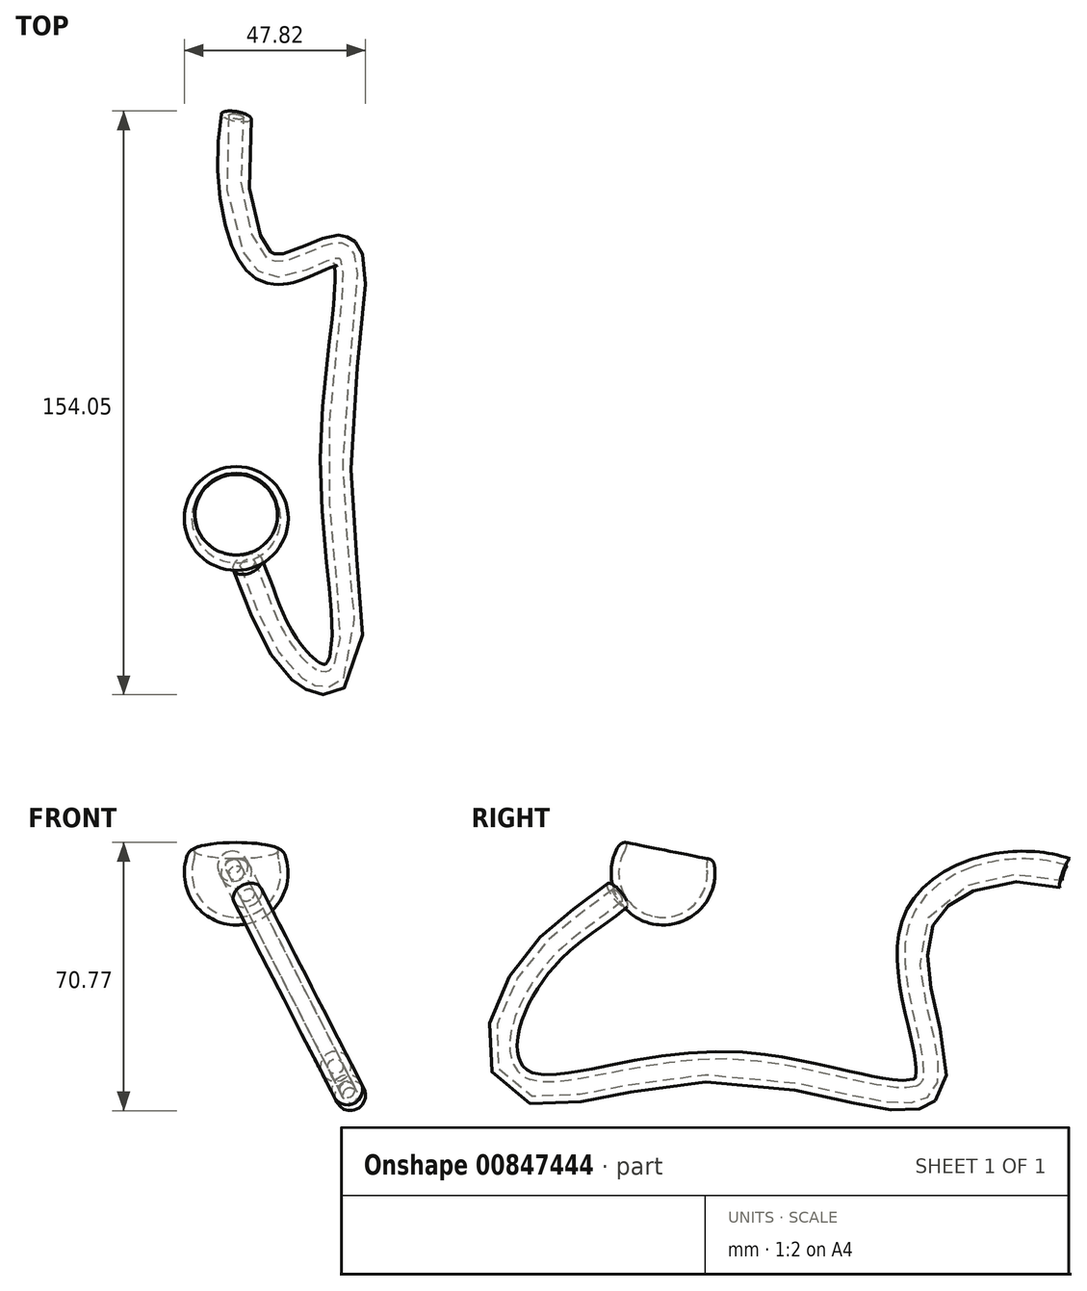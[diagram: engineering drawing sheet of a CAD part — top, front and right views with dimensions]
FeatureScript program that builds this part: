
annotation { "Feature Type Name" : "Feature", "Feature Type Description" : "" }
export const myFeature = defineFeature(function(context is Context, id is Id, definition is map)
    precondition{}
    {
        {
            var Q0;
            Q0=qCreatedBy(makeId("Right.planeOp"),FACE);
            var sketch = newSketch(context, id + "F0", { "sketchPlane" : qUnion([Q0])});
            skArc(sketch, "E0", {"start": v(-39.77, 2.1) * mm, "mid": v(-55.97, -13.44) * mm, "end": v(-65.04, 7.1) * mm});
            skLineSegment(sketch, "E1", {"start": v(-62.94, 8.02) * mm, "end": v(-41.36, 3.75) * mm});
            skPoint(sketch, "E2.visualSharp", {"position": v(-64.23, 8.28) * mm});
            skArc(sketch, "E2.filletArc", {"start": v(-62.94, 8.02) * mm, "mid": v(-64.13, 7.89) * mm, "end": v(-65.04, 7.1) * mm});
            skPoint(sketch, "E3.visualSharp", {"position": v(-40.06, 3.5) * mm});
            skArc(sketch, "E3.filletArc", {"start": v(-39.77, 2.1) * mm, "mid": v(-40.3, 3.17) * mm, "end": v(-41.36, 3.75) * mm});
            skLineSegment(sketch, "E4", {"start": v(-53.31, 0) * mm, "end": v(-55.97, -13.44) * mm, "construction": true});
            skLineSegment(sketch, "E5", {"start": v(-52.15, 5.89) * mm, "end": v(-55.97, -13.44) * mm});
            skSolve(sketch);
        }
        {
            var Q0;
            {var subQ0=sQuery(id+"F0.wireOp",EDGE,"E3.filletArc");Q0=makeQuery(id+"F0.imprint","IMPRINT",FACE,{"disambiguationData":[TD([[makeQuery(id+"F0.imprint","IMPRINT",EDGE,{"derivedFrom":subQ0}),1.0]])]});}
            var Q1;
            Q1=sQuery(id+"F0.wireOp",EDGE,"E5");
            revolve(context, id + "F1", {"surfaceOperationType" : NewSurfaceOperationType.NEW, "entities" : qUnion([Q0]), "axis" : qUnion([Q1]), "revolveType" : RevolveType.FULL});
        }
        {
            var Q0;
            Q0=makeQuery(id+"F1.opRevolve","SWEPT_FACE",FACE,{"disambiguationData":[OSD([sQuery(id+"F0.wireOp",EDGE,"E1")])]});
            shell(context, id + "F2", {"entities" : qUnion([Q0]), "thickness" : 2 * mm});
        }
        {
            var Q0;
            Q0=makeQuery(id+"F2.opShell","OFFSET_EDGE",EDGE,{"disambiguationData":[OSD([sQuery(id+"F0.wireOp",EDGE,"E0"),sQuery(id+"F0.wireOp",EDGE,"E1"),sQuery(id+"F0.wireOp",EDGE,"E3.filletArc")])]});
            fillet(context, id + "F3", {"entities" : qUnion([Q0]), "radius" : 5 * mm, "tangentPropagation" : true, "allowEdgeOverflow" : false});
        }
        {
            var Q0;
            Q0=qCreatedBy(makeId("Front.planeOp"),FACE);
            var sketch = newSketch(context, id + "F4", { "sketchPlane" : qUnion([Q0])});
            skLineSegment(sketch, "E6", {"start": v(19.4, 37.82) * mm, "end": v(-19.4, -37.82) * mm});
            skLineSegment(sketch, "E7", {"start": v(-19.4, 37.82) * mm, "end": v(19.4, -37.82) * mm});
            skPoint(sketch, "E8", {"position": v(0, 0) * mm});
            skSolve(sketch);
        }
        {
            var Q0;
            Q0=sQuery(id+"F4.wireOp",EDGE,"E7");
            cPlane(context, id + "F5", {"entities" : qUnion([Q0]), "cplaneType" : CPlaneType.LINE_ANGLE, "offset" : 25 * mm, "angle" : 0 * degree, "width" : 150 * mm, "height" : 150 * mm});
        }
        {
            var Q0;
            Q0=qCreatedBy(makeId("Right.planeOp"),FACE);
            var sketch = newSketch(context, id + "F6", { "sketchPlane" : qUnion([Q0])});
            skLineSegment(sketch, "E9", {"start": v(-100.5, -56.65) * mm, "end": v(83.38, -56.65) * mm});
            skSolve(sketch);
        }
        {
            var Q0;
            Q0=sQuery(id+"F6.wireOp",EDGE,"E9");
            cPlane(context, id + "F7", {"entities" : qUnion([Q0]), "cplaneType" : CPlaneType.LINE_ANGLE, "offset" : 25 * mm, "angle" : 0 * degree, "width" : 150 * mm, "height" : 150 * mm});
        }
        {
            var Q0;
            Q0=qCreatedBy(id+"F5.planeOp",FACE);
            var sketch = newSketch(context, id + "F8", { "sketchPlane" : qUnion([Q0])});
            skArc(sketch, "E10", {"start": v(39.81, 2.36) * mm, "mid": v(56.29, -13.38) * mm, "end": v(64.54, 7.86) * mm, "construction": true});
            skFitSpline(sketch, "E11", {"points": [v(65.35, -6.55) * mm, v(83.37, -22.7) * mm, v(95.76, -49.5) * mm, v(88.47, -63.68) * mm, v(34.3, -57.51) * mm, v(-16.29, -63.68) * mm, v(-13.75, -14.92) * mm, v(-52.76, 0) * mm], "startDerivative": vector(170.47, -160.45) * mm, "endDerivative": vector(-268.82, -105.7) * mm});
            skSolve(sketch);
        }
        {
            var Q0;
            Q0=sQuery(id+"F8.wireOp",VERTEX,"E11.end");
            var Q1;
            Q1=sQuery(id+"F8.wireOp",EDGE,"E11");
            cPlane(context, id + "F9", {"entities" : qUnion([Q0, Q1]), "cplaneType" : CPlaneType.CURVE_POINT, "offset" : 25 * mm, "width" : 150 * mm, "height" : 150 * mm});
        }
        {
            var Q0;
            Q0=qCreatedBy(id+"F9.planeOp",FACE);
            var sketch = newSketch(context, id + "F10", { "sketchPlane" : qUnion([Q0])});
            skCircle(sketch, "E12", {"center": v(8.32, 17.42) * mm, "radius": 4 * mm});
            skCircle(sketch, "E13", {"center": v(8.32, 17.42) * mm, "radius": 2 * mm});
            skSolve(sketch);
        }
        {
            var Q0;
            Q0=makeQuery(id+"F10.imprint","IMPRINT",FACE,{"disambiguationData":[TD([[makeQuery(id+"F10.imprint","IMPRINT",EDGE,{"derivedFrom":sQuery(id+"F10.wireOp",EDGE,"E12")}),1.0]])]});
            var Q1;
            Q1 = qConstructionFilter(qBodyType(qCreatedBy(id + "F8" ,EDGE), BodyType.WIRE), ConstructionObject.NO);
            sweep(context, id + "F11", {"profiles" : qUnion([Q0]), "path" : qUnion([Q1])});
        }
    });
